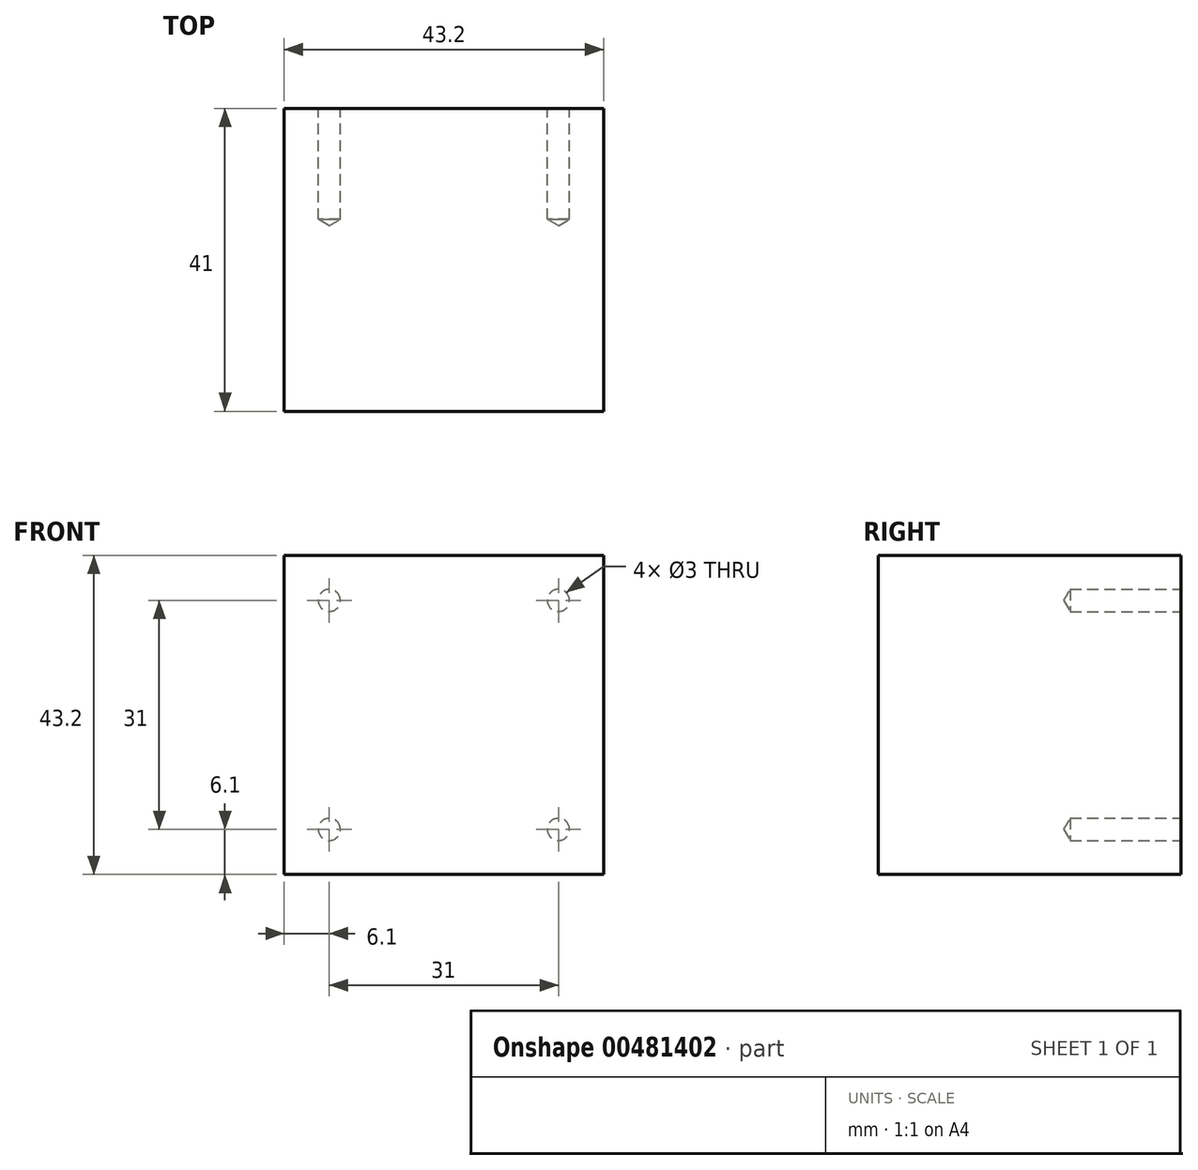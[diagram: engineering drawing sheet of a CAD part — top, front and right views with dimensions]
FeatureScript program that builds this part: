
annotation { "Feature Type Name" : "Feature", "Feature Type Description" : "" }
export const myFeature = defineFeature(function(context is Context, id is Id, definition is map)
    precondition{}
    {
        {
            var Q0;
            Q0=qCreatedBy(makeId("Front.planeOp"),FACE);
            var sketch = newSketch(context, id + "F0", { "sketchPlane" : qUnion([Q0])});
            skLineSegment(sketch, "E0.bottom", {"start": v(0, 0) * mm, "end": v(43.2, 0) * mm});
            skLineSegment(sketch, "E0.top", {"start": v(0, -43.2) * mm, "end": v(43.2, -43.2) * mm});
            skLineSegment(sketch, "E0.left", {"start": v(0, 0) * mm, "end": v(0, -43.2) * mm});
            skLineSegment(sketch, "E0.right", {"start": v(43.2, 0) * mm, "end": v(43.2, -43.2) * mm});
            skLineSegment(sketch, "E1", {"start": v(0, 0) * mm, "end": v(43.2, -43.2) * mm, "construction": true});
            skLineSegment(sketch, "E2", {"start": v(43.2, 0) * mm, "end": v(0, -43.2) * mm, "construction": true});
            skPoint(sketch, "E3", {"position": v(6.1, -6.1) * mm});
            skPoint(sketch, "E4", {"position": v(37.1, -6.1) * mm});
            skPoint(sketch, "E5", {"position": v(37.1, -37.1) * mm});
            skPoint(sketch, "E6", {"position": v(6.1, -37.1) * mm});
            skSolve(sketch);
        }
        {
            var Q0;
            Q0=makeQuery(id+"F0.imprint","IMPRINT",FACE,{"disambiguationData":[TD([[makeQuery(id+"F0.imprint","IMPRINT",EDGE,{"derivedFrom":sQuery(id+"F0.wireOp",EDGE,"E0.bottom")}),-1.0]])]});
            extrude(context, id + "F1", {"entities" : qUnion([Q0]), "depth" : 41 * mm});
        }
        {
            var Q0;
            Q0=sQuery(id+"F0.wireOp",VERTEX,"E4");
            var Q1;
            Q1=sQuery(id+"F0.wireOp",VERTEX,"E3");
            var Q2;
            Q2=sQuery(id+"F0.wireOp",VERTEX,"E6");
            var Q3;
            Q3=sQuery(id+"F0.wireOp",VERTEX,"E5");
            var Q4;
            Q4=makeQuery(id+"F1.opExtrude","SWEPT_BODY",BODY,{"disambiguationData":[OSD([sQuery(id+"F0.wireOp",EDGE,"E0.bottom"),sQuery(id+"F0.wireOp",EDGE,"E0.top"),sQuery(id+"F0.wireOp",EDGE,"E0.left"),sQuery(id+"F0.wireOp",EDGE,"E0.right")])]});
            hole(context, id + "F2", {"style" : HoleStyle.SIMPLE, "endStyle" : HoleEndStyle.BLIND, "oppositeDirection" : true, "holeDiameter" : 3 * mm, "holeDepth" : 15 * mm, "tappedDepth" : 12 * mm, "tapClearance" : 3, "locations" : qUnion([Q0, Q1, Q2, Q3]), "scope" : qUnion([Q4])});
        }
    });
